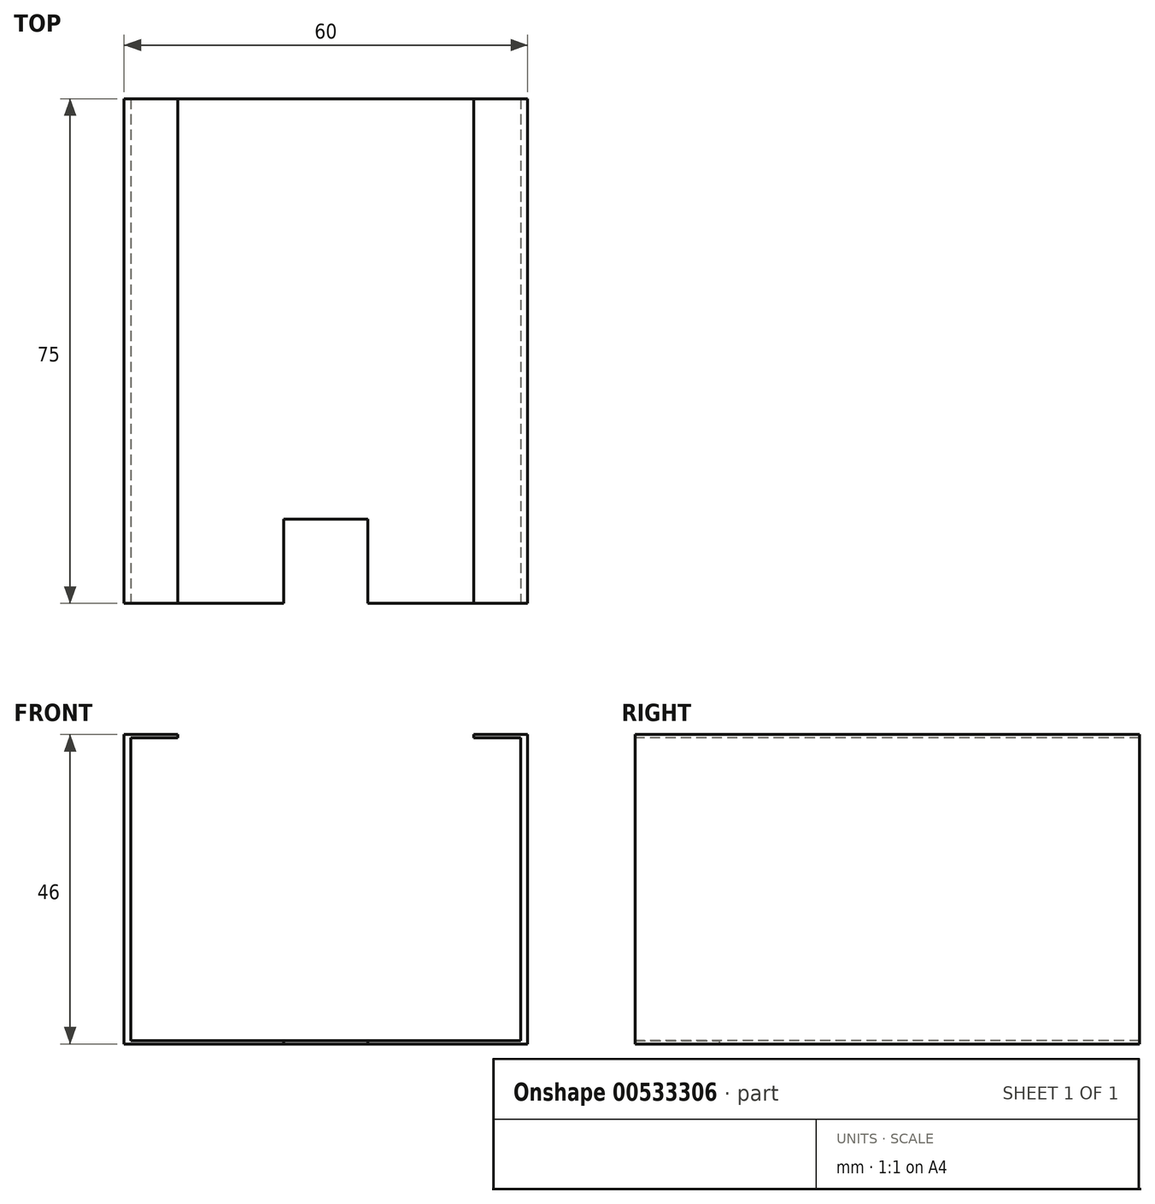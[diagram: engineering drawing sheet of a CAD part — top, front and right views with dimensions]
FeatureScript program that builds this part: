
annotation { "Feature Type Name" : "Feature", "Feature Type Description" : "" }
export const myFeature = defineFeature(function(context is Context, id is Id, definition is map)
    precondition{}
    {
        {
            var Q0;
            Q0=qCreatedBy(makeId("Top.planeOp"),FACE);
            var sketch = newSketch(context, id + "F0", { "sketchPlane" : qUnion([Q0])});
            skLineSegment(sketch, "E0.bottom", {"start": v(-28.08, 33.83) * mm, "end": v(31.92, 33.83) * mm});
            skLineSegment(sketch, "E0.top", {"start": v(-28.08, -41.17) * mm, "end": v(31.92, -41.17) * mm});
            skLineSegment(sketch, "E0.left", {"start": v(-28.08, 33.83) * mm, "end": v(-28.08, -41.17) * mm});
            skLineSegment(sketch, "E0.right", {"start": v(31.92, 33.83) * mm, "end": v(31.92, -41.17) * mm});
            skSolve(sketch);
        }
        {
            var Q0;
            Q0=makeQuery(id+"F0.imprint","IMPRINT",FACE,{"disambiguationData":[TD([[makeQuery(id+"F0.imprint","IMPRINT",EDGE,{"derivedFrom":sQuery(id+"F0.wireOp",EDGE,"E0.bottom")}),-1.0]])]});
            extrude(context, id + "F1", {"entities" : qUnion([Q0]), "depth" : 0.5 * mm, "offsetDistance" : 25 * mm});
        }
        {
            var Q0;
            Q0=makeQuery(id+"F1.opExtrude","CAP_FACE",FACE,{"disambiguationData":[OSD([sQuery(id+"F0.wireOp",EDGE,"E0.bottom"),sQuery(id+"F0.wireOp",EDGE,"E0.top"),sQuery(id+"F0.wireOp",EDGE,"E0.left"),sQuery(id+"F0.wireOp",EDGE,"E0.right")])],"isStart":false});
            var sketch = newSketch(context, id + "F2", { "sketchPlane" : qUnion([Q0])});
            skLineSegment(sketch, "E1.bottom", {"start": v(-28.08, 33.83) * mm, "end": v(-27.08, 33.83) * mm});
            skLineSegment(sketch, "E1.top", {"start": v(-28.08, -41.17) * mm, "end": v(-27.08, -41.17) * mm});
            skLineSegment(sketch, "E1.left", {"start": v(-28.08, 33.83) * mm, "end": v(-28.08, -41.17) * mm});
            skLineSegment(sketch, "E1.right", {"start": v(-27.08, 33.83) * mm, "end": v(-27.08, -41.17) * mm});
            skLineSegment(sketch, "E2.bottom", {"start": v(31.92, 33.83) * mm, "end": v(30.92, 33.83) * mm});
            skLineSegment(sketch, "E2.top", {"start": v(31.92, -41.17) * mm, "end": v(30.92, -41.17) * mm});
            skLineSegment(sketch, "E2.left", {"start": v(31.92, 33.83) * mm, "end": v(31.92, -41.17) * mm});
            skLineSegment(sketch, "E2.right", {"start": v(30.92, 33.83) * mm, "end": v(30.92, -41.17) * mm});
            skSolve(sketch);
        }
        {
            var Q0;
            Q0 = qSketchRegion(id + "F2", true);
            extrude(context, id + "F3", {"entities" : qUnion([Q0]), "operationType" : NewBodyOperationType.ADD, "depth" : 45 * mm, "offsetDistance" : 25 * mm});
        }
        {
            var Q0;
            Q0=makeQuery(id+"F3.opExtrude","CAP_FACE",FACE,{"disambiguationData":[OSD([sQuery(id+"F2.wireOp",EDGE,"E1.bottom"),sQuery(id+"F2.wireOp",EDGE,"E1.top"),sQuery(id+"F2.wireOp",EDGE,"E1.left"),sQuery(id+"F2.wireOp",EDGE,"E1.right")])],"isStart":false});
            var sketch = newSketch(context, id + "F4", { "sketchPlane" : qUnion([Q0])});
            skLineSegment(sketch, "E3.bottom", {"start": v(-28.08, 33.83) * mm, "end": v(-20.08, 33.83) * mm});
            skLineSegment(sketch, "E3.top", {"start": v(-28.08, -41.17) * mm, "end": v(-20.08, -41.17) * mm});
            skLineSegment(sketch, "E3.left", {"start": v(-28.08, 33.83) * mm, "end": v(-28.08, -41.17) * mm});
            skLineSegment(sketch, "E3.right", {"start": v(-20.08, 33.83) * mm, "end": v(-20.08, -41.17) * mm});
            skLineSegment(sketch, "E4.bottom", {"start": v(31.92, 33.83) * mm, "end": v(23.92, 33.83) * mm});
            skLineSegment(sketch, "E4.top", {"start": v(31.92, -41.17) * mm, "end": v(23.92, -41.17) * mm});
            skLineSegment(sketch, "E4.left", {"start": v(31.92, 33.83) * mm, "end": v(31.92, -41.17) * mm});
            skLineSegment(sketch, "E4.right", {"start": v(23.92, 33.83) * mm, "end": v(23.92, -41.17) * mm});
            skSolve(sketch);
        }
        {
            var Q0;
            Q0 = qSketchRegion(id + "F4", true);
            extrude(context, id + "F5", {"entities" : qUnion([Q0]), "operationType" : NewBodyOperationType.ADD, "depth" : 0.5 * mm, "offsetDistance" : 25 * mm});
        }
        {
            var Q0;
            Q0=makeQuery(id+"F1.opExtrude","CAP_FACE",FACE,{"disambiguationData":[OSD([sQuery(id+"F0.wireOp",EDGE,"E0.bottom"),sQuery(id+"F0.wireOp",EDGE,"E0.top"),sQuery(id+"F0.wireOp",EDGE,"E0.left"),sQuery(id+"F0.wireOp",EDGE,"E0.right")])],"isStart":true});
            var sketch = newSketch(context, id + "F6", { "sketchPlane" : qUnion([Q0])});
            skLineSegment(sketch, "E5.bottom", {"start": v(-4.33, 41.17) * mm, "end": v(8.17, 41.17) * mm});
            skLineSegment(sketch, "E5.top", {"start": v(-4.33, 28.67) * mm, "end": v(8.17, 28.67) * mm});
            skLineSegment(sketch, "E5.left", {"start": v(-4.33, 41.17) * mm, "end": v(-4.33, 28.67) * mm});
            skLineSegment(sketch, "E5.right", {"start": v(8.17, 41.17) * mm, "end": v(8.17, 28.67) * mm});
            skLineSegment(sketch, "E6", {"start": v(8.17, 38.09) * mm, "end": v(31.92, 38.09) * mm, "construction": true});
            skLineSegment(sketch, "E7", {"start": v(-4.33, 37.68) * mm, "end": v(-28.08, 37.68) * mm, "construction": true});
            skSolve(sketch);
        }
        {
            var Q0;
            Q0=makeQuery(id+"F6.imprint","IMPRINT",FACE,{"disambiguationData":[TD([[makeQuery(id+"F6.imprint","IMPRINT",EDGE,{"derivedFrom":sQuery(id+"F6.wireOp",EDGE,"E5.bottom")}),-1.0]])]});
            extrude(context, id + "F7", {"entities" : qUnion([Q0]), "operationType" : NewBodyOperationType.REMOVE, "endBound" : BoundingType.UP_TO_NEXT, "oppositeDirection" : true, "depth" : 25 * mm, "offsetDistance" : 25 * mm});
        }
    });
